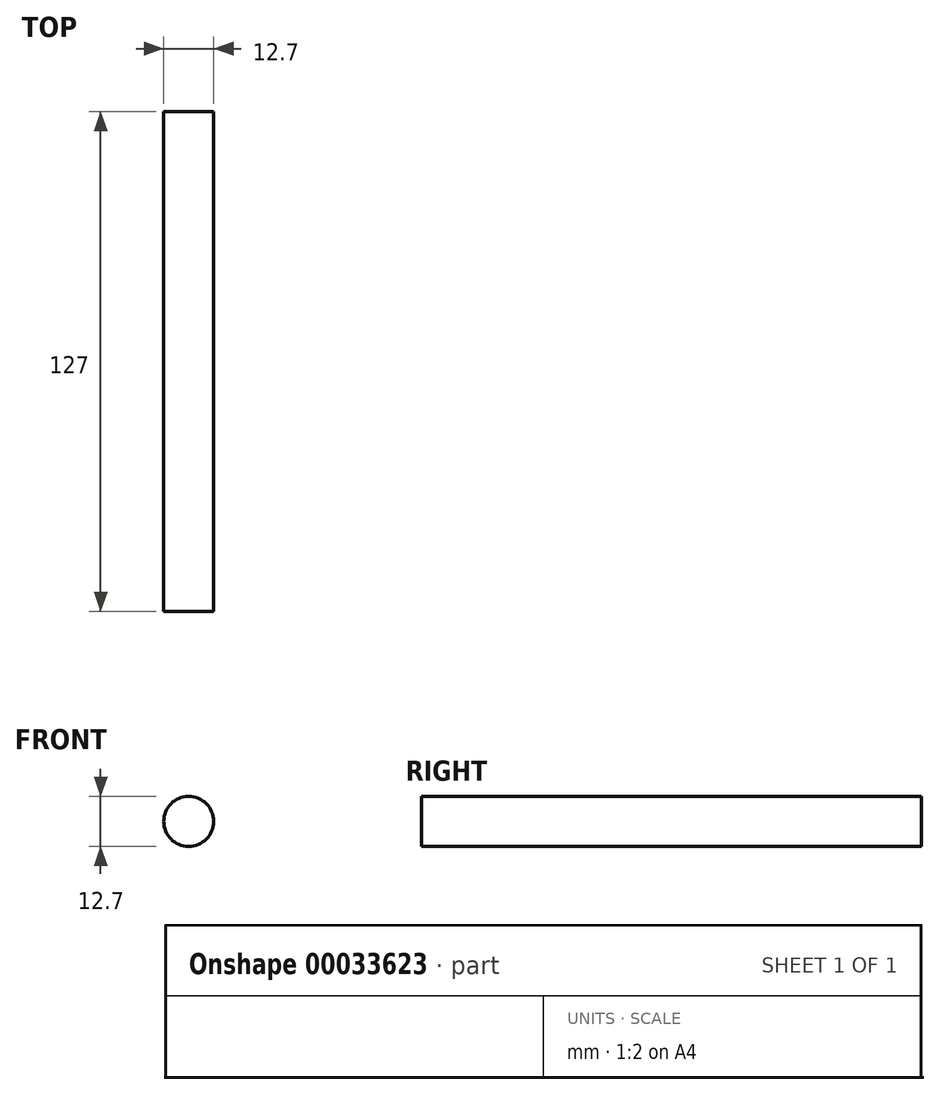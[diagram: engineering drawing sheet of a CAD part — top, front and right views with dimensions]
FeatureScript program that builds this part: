
annotation { "Feature Type Name" : "Feature", "Feature Type Description" : "" }
export const myFeature = defineFeature(function(context is Context, id is Id, definition is map)
    precondition{}
    {
        {
            var Q0;
            Q0=qCreatedBy(makeId("Front.planeOp"),FACE);
            var sketch = newSketch(context, id + "F0", { "sketchPlane" : qUnion([Q0])});
            skCircle(sketch, "E0", {"center": v(0, 0) * mm, "radius": 6.35 * mm});
            skSolve(sketch);
        }
        {
            var Q0;
            Q0=makeQuery(id+"F0.imprint","IMPRINT",FACE,{"disambiguationData":[TD([[makeQuery(id+"F0.imprint","IMPRINT",EDGE,{"derivedFrom":sQuery(id+"F0.wireOp",EDGE,"E0")}),1.0]])]});
            extrude(context, id + "F1", {"entities" : qUnion([Q0]), "depth" : 127 * mm});
        }
    });
